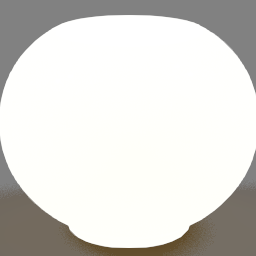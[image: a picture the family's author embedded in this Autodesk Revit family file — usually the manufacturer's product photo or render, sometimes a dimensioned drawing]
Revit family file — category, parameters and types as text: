
# Revit family: 3-050X-xx Track Mirror
name_source: partatom
category: Lighting Fixtures
units: mm (PartAtom-declared; Revit-internal decimal feet)

## family parameters
Always vertical = Yes
Cut with Voids When Loaded = No
Host = Wall
Light Source = No
OmniClass Number = 23.80.70.00
OmniClass Title = Lighting
Part Type = Normal
Room Calculation Point = No
Round Connector Dimension = Use Diameter
Shared = No

## types (7) — shared parameters
Diffuser = Ghost Mirror
Lamp = LED Array
Manufacturer = Vanita by Oxygen
Metal Finish 1 = 15 - Black
Model = 3-050X-xx / Track
References = Ref. 3 = 120 V / Ref. 37 = 277 V
URL = www.oxygenlighting.com
Voltage = 120 V
Voltage Input = 120 V or 277 V - 50/60 Hz
zero-valued in all types: Default Elevation

## per-type parameters (varying)
| type | Height | Wattage Comments | Width |
| 3-0501-15 / Black | 610 mm  [stored 2.00131 ft] | 1 x 78 W at 120 V | 457 mm  [stored 1.49934 ft] |
| 3-0503-15 / Black | 610 mm  [stored 2.00131 ft] | 1 x 124.5 W at 120 V | 914 mm  [stored 2.99869 ft] |
| 3-0504-15 / Black | 914 mm  [stored 2.99869 ft] | 1 x 165.1 W at 120 V | 914 mm  [stored 2.99869 ft] |
| 3-0505-15 / Black | 914 mm  [stored 2.99869 ft] | 1 x 170.7 W at 120 V | 1219 mm |
| 3-0502-15 / Black | 914 mm  [stored 2.99869 ft] | 1 x 102.7 W at 120 V | 610 mm  [stored 2.00131 ft] |
| 3-0506-15 / Black | 1219 mm | 1 x 170.7 W at 120 V | 1219 mm |
| 3-0507-15 / Black | 1067 mm  [stored 3.50066 ft] | 1 x 170.7 W at 120 V | 1524 mm  [stored 5 ft] |

note: [stored X ft] marks values corroborated as IEEE doubles in the binary element streams (Revit-internal decimal feet)

## geometry (parser evidence)
native form markers: Sweep x6
no freeform markers — native parametric forms only
